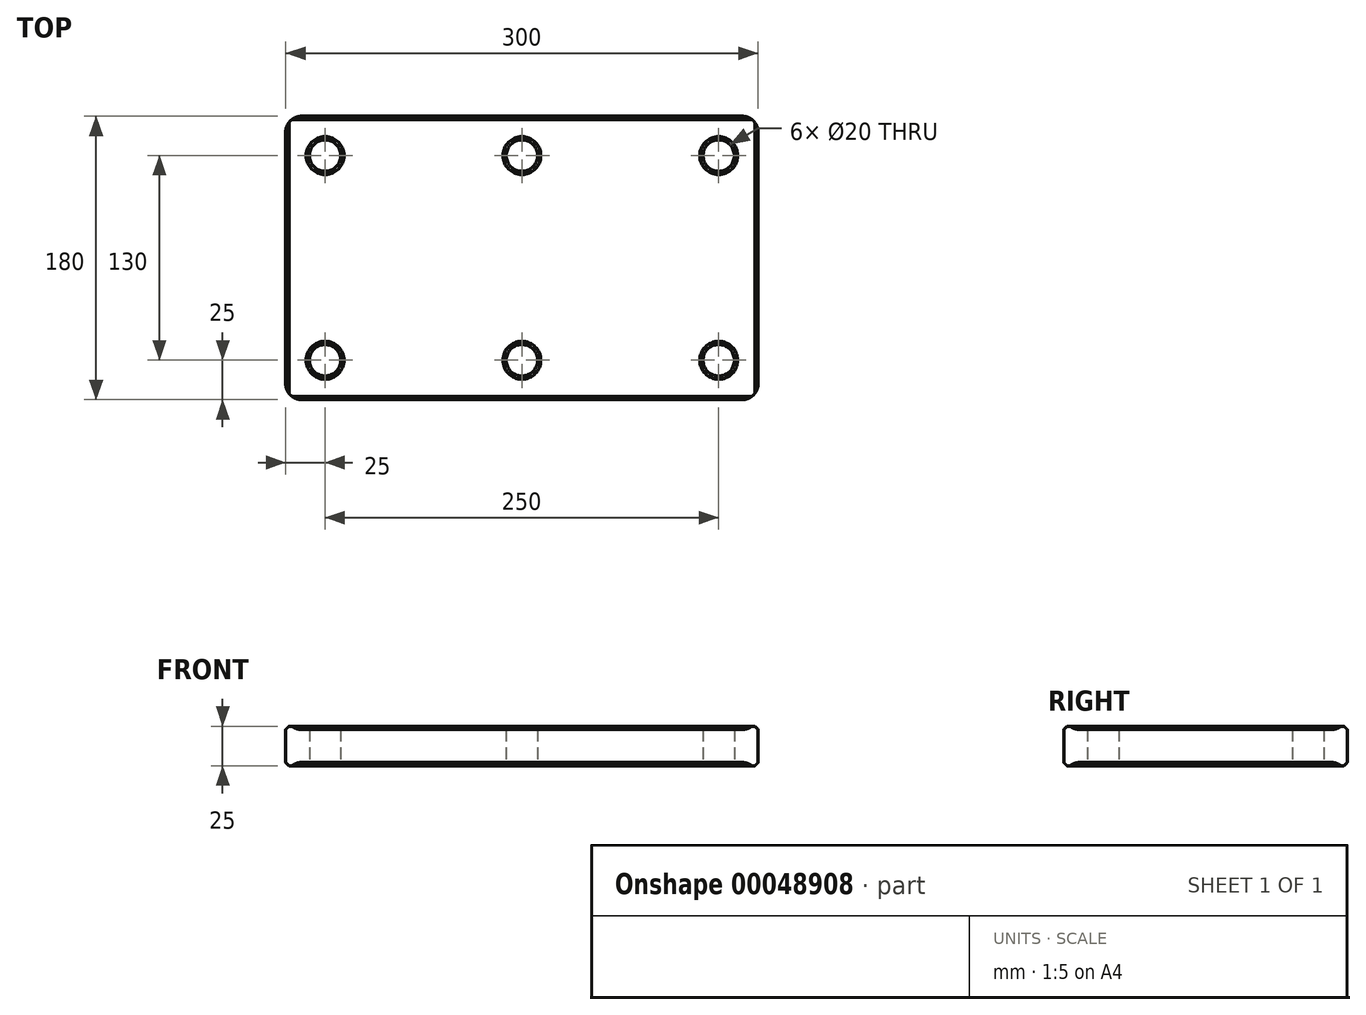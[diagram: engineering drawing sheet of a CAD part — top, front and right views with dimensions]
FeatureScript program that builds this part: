
annotation { "Feature Type Name" : "Feature", "Feature Type Description" : "" }
export const myFeature = defineFeature(function(context is Context, id is Id, definition is map)
    precondition{}
    {
        {
            var Q0;
            Q0=qCreatedBy(makeId("Top.planeOp"),FACE);
            var sketch = newSketch(context, id + "F0", { "sketchPlane" : qUnion([Q0])});
            skLineSegment(sketch, "E0.rect.bottom", {"start": v(-150, 90) * mm, "end": v(150, 90) * mm});
            skLineSegment(sketch, "E0.rect.top", {"start": v(-150, -90) * mm, "end": v(150, -90) * mm});
            skLineSegment(sketch, "E0.rect.left", {"start": v(-150, 90) * mm, "end": v(-150, -90) * mm});
            skLineSegment(sketch, "E0.rect.right", {"start": v(150, 90) * mm, "end": v(150, -90) * mm});
            skPoint(sketch, "E0.rect.middle", {"position": v(0, 0) * mm});
            skLineSegment(sketch, "E1.rect.bottom", {"start": v(-125, 65) * mm, "end": v(125, 65) * mm, "construction": true});
            skLineSegment(sketch, "E1.rect.top", {"start": v(-125, -65) * mm, "end": v(125, -65) * mm, "construction": true});
            skLineSegment(sketch, "E1.rect.left", {"start": v(-125, 65) * mm, "end": v(-125, -65) * mm, "construction": true});
            skLineSegment(sketch, "E1.rect.right", {"start": v(125, 65) * mm, "end": v(125, -65) * mm, "construction": true});
            skCircle(sketch, "E2", {"center": v(-125, 65) * mm, "radius": 10 * mm});
            skCircle(sketch, "E3", {"center": v(0, 65) * mm, "radius": 10 * mm});
            skLineSegment(sketch, "E4", {"start": v(0, 65) * mm, "end": v(0, -65) * mm, "construction": true});
            skCircle(sketch, "E5.MirrorC", {"center": v(125, 65) * mm, "radius": 10 * mm});
            skLineSegment(sketch, "E6", {"start": v(-61.57, 0) * mm, "end": v(56.25, 0) * mm, "construction": true});
            skCircle(sketch, "E7.MirrorC", {"center": v(-125, -65) * mm, "radius": 10 * mm});
            skCircle(sketch, "E8.MirrorC", {"center": v(0, -65) * mm, "radius": 10 * mm});
            skCircle(sketch, "E9.MirrorC", {"center": v(125, -65) * mm, "radius": 10 * mm});
            skSolve(sketch);
        }
        {
            var Q0;
            Q0=makeQuery(id+"F0.imprint","IMPRINT",FACE,{"disambiguationData":[TD([[makeQuery(id+"F0.imprint","IMPRINT",EDGE,{"derivedFrom":sQuery(id+"F0.wireOp",EDGE,"E0.rect.bottom")}),-1.0]])]});
            extrude(context, id + "F1", {"entities" : qUnion([Q0]), "depth" : 25 * mm});
        }
        {
            var Q0;
            Q0=makeQuery(id+"F1.opExtrude","CAP_EDGE",EDGE,{"disambiguationData":[OSD([sQuery(id+"F0.wireOp",EDGE,"E7.MirrorC")])],"isStart":false});
            var Q1;
            Q1=makeQuery(id+"F1.opExtrude","CAP_EDGE",EDGE,{"disambiguationData":[OSD([sQuery(id+"F0.wireOp",EDGE,"E2")])],"isStart":false});
            var Q2;
            Q2=makeQuery(id+"F1.opExtrude","CAP_EDGE",EDGE,{"disambiguationData":[OSD([sQuery(id+"F0.wireOp",EDGE,"E8.MirrorC")])],"isStart":false});
            var Q3;
            Q3=makeQuery(id+"F1.opExtrude","CAP_EDGE",EDGE,{"disambiguationData":[OSD([sQuery(id+"F0.wireOp",EDGE,"E3")])],"isStart":false});
            var Q4;
            Q4=makeQuery(id+"F1.opExtrude","CAP_EDGE",EDGE,{"disambiguationData":[OSD([sQuery(id+"F0.wireOp",EDGE,"E5.MirrorC")])],"isStart":false});
            var Q5;
            Q5=makeQuery(id+"F1.opExtrude","CAP_EDGE",EDGE,{"disambiguationData":[OSD([sQuery(id+"F0.wireOp",EDGE,"E9.MirrorC")])],"isStart":false});
            var Q6;
            Q6=makeQuery(id+"F1.opExtrude","CAP_EDGE",EDGE,{"disambiguationData":[OSD([sQuery(id+"F0.wireOp",EDGE,"E0.rect.left")])],"isStart":false});
            var Q7;
            Q7=makeQuery(id+"F1.opExtrude","CAP_EDGE",EDGE,{"disambiguationData":[OSD([sQuery(id+"F0.wireOp",EDGE,"E0.rect.left")])],"isStart":true});
            var Q8;
            Q8=makeQuery(id+"F1.opExtrude","CAP_EDGE",EDGE,{"disambiguationData":[OSD([sQuery(id+"F0.wireOp",EDGE,"E0.rect.right")])],"isStart":false});
            var Q9;
            Q9=makeQuery(id+"F1.opExtrude","CAP_EDGE",EDGE,{"disambiguationData":[OSD([sQuery(id+"F0.wireOp",EDGE,"E0.rect.right")])],"isStart":true});
            chamfer(context, id + "F2", {"entities" : qUnion([Q0, Q1, Q2, Q3, Q4, Q5, Q6, Q7, Q8, Q9]), "chamferType" : ChamferType.OFFSET_ANGLE, "width" : 2 * mm, "oppositeDirection" : false, "angle" : 45 * degree, "tangentPropagation" : true});
        }
        {
            var Q0;
            Q0=makeQuery(id+"F1.opExtrude","CAP_EDGE",EDGE,{"disambiguationData":[OSD([sQuery(id+"F0.wireOp",EDGE,"E0.rect.top")])],"isStart":false});
            var Q1;
            Q1=makeQuery(id+"F1.opExtrude","CAP_EDGE",EDGE,{"disambiguationData":[OSD([sQuery(id+"F0.wireOp",EDGE,"E0.rect.top")])],"isStart":true});
            var Q2;
            Q2=makeQuery(id+"F1.opExtrude","CAP_EDGE",EDGE,{"disambiguationData":[OSD([sQuery(id+"F0.wireOp",EDGE,"E0.rect.bottom")])],"isStart":false});
            var Q3;
            Q3=makeQuery(id+"F1.opExtrude","CAP_EDGE",EDGE,{"disambiguationData":[OSD([sQuery(id+"F0.wireOp",EDGE,"E0.rect.bottom")])],"isStart":true});
            chamfer(context, id + "F3", {"entities" : qUnion([Q0, Q1, Q2, Q3]), "chamferType" : ChamferType.OFFSET_ANGLE, "width" : 2 * mm, "oppositeDirection" : false, "angle" : 45 * degree, "tangentPropagation" : true});
        }
        {
            var Q0;
            Q0=makeQuery(id+"F1.opExtrude","SWEPT_EDGE",EDGE,{"disambiguationData":[OSD([sQuery(id+"F0.wireOp",EDGE,"E0.rect.top"),sQuery(id+"F0.wireOp",EDGE,"E0.rect.right")])]});
            var Q1;
            Q1=makeQuery(id+"F1.opExtrude","SWEPT_EDGE",EDGE,{"disambiguationData":[OSD([sQuery(id+"F0.wireOp",EDGE,"E0.rect.top"),sQuery(id+"F0.wireOp",EDGE,"E0.rect.left")])]});
            var Q2;
            Q2=makeQuery(id+"F1.opExtrude","SWEPT_EDGE",EDGE,{"disambiguationData":[OSD([sQuery(id+"F0.wireOp",EDGE,"E0.rect.bottom"),sQuery(id+"F0.wireOp",EDGE,"E0.rect.left")])]});
            var Q3;
            Q3=makeQuery(id+"F1.opExtrude","SWEPT_EDGE",EDGE,{"disambiguationData":[OSD([sQuery(id+"F0.wireOp",EDGE,"E0.rect.bottom"),sQuery(id+"F0.wireOp",EDGE,"E0.rect.right")])]});
            fillet(context, id + "F4", {"entities" : qUnion([Q0, Q1, Q2, Q3]), "radius" : 10 * mm, "tangentPropagation" : true, "allowEdgeOverflow" : false});
        }
    });
